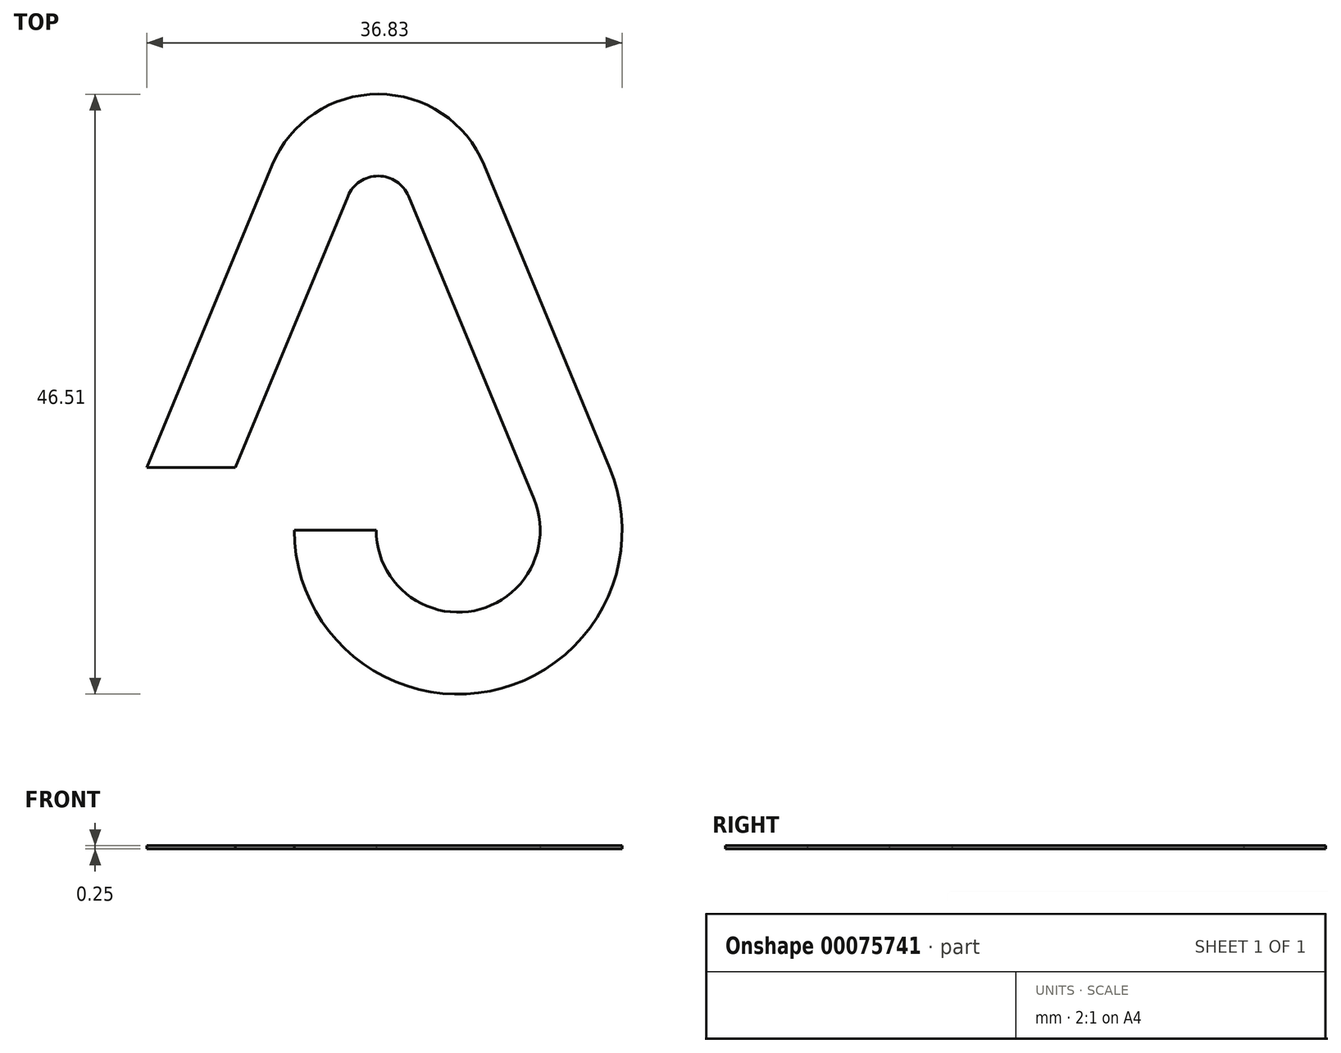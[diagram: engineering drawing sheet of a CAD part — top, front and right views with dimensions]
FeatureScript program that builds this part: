
annotation { "Feature Type Name" : "Feature", "Feature Type Description" : "" }
export const myFeature = defineFeature(function(context is Context, id is Id, definition is map)
    precondition{}
    {
        {
            var Q0;
            Q0=qCreatedBy(makeId("Top.planeOp"),FACE);
            var sketch = newSketch(context, id + "F0", { "sketchPlane" : qUnion([Q0])});
            skLineSegment(sketch, "E0", {"start": v(-39.76, -5.74) * mm, "end": v(-30.04, 17.73) * mm});
            skLineSegment(sketch, "E1", {"start": v(-13.61, 17.73) * mm, "end": v(-3.9, -5.74) * mm});
            skArc(sketch, "E2", {"start": v(-30.04, 17.73) * mm, "mid": v(-21.83, 23.21) * mm, "end": v(-13.61, 17.73) * mm});
            skLineSegment(sketch, "E3", {"start": v(-32.89, -5.74) * mm, "end": v(-24.17, 15.3) * mm});
            skLineSegment(sketch, "E4", {"start": v(-19.48, 15.3) * mm, "end": v(-9.76, -8.17) * mm});
            skArc(sketch, "E5", {"start": v(-24.17, 15.3) * mm, "mid": v(-21.83, 16.86) * mm, "end": v(-19.48, 15.3) * mm});
            skArc(sketch, "E6", {"start": v(-9.76, -8.17) * mm, "mid": v(-14.39, -16.83) * mm, "end": v(-21.98, -10.6) * mm});
            skArc(sketch, "E7", {"start": v(-3.9, -5.74) * mm, "mid": v(-13.15, -23.06) * mm, "end": v(-28.33, -10.6) * mm});
            skLineSegment(sketch, "E8", {"start": v(-32.89, -5.74) * mm, "end": v(-39.76, -5.74) * mm});
            skLineSegment(sketch, "E9", {"start": v(-21.98, -10.6) * mm, "end": v(-28.33, -10.6) * mm});
            skSolve(sketch);
        }
        {
            var Q0;
            Q0=makeQuery(id+"F0.imprint","IMPRINT",FACE,{"disambiguationData":[TD([[makeQuery(id+"F0.imprint","IMPRINT",EDGE,{"derivedFrom":sQuery(id+"F0.wireOp",EDGE,"E0")}),-1.0]])]});
            extrude(context, id + "F1", {"entities" : qUnion([Q0]), "offsetDistance" : 25.4 * mm, "depth" : 0.25 * mm});
        }
    });
